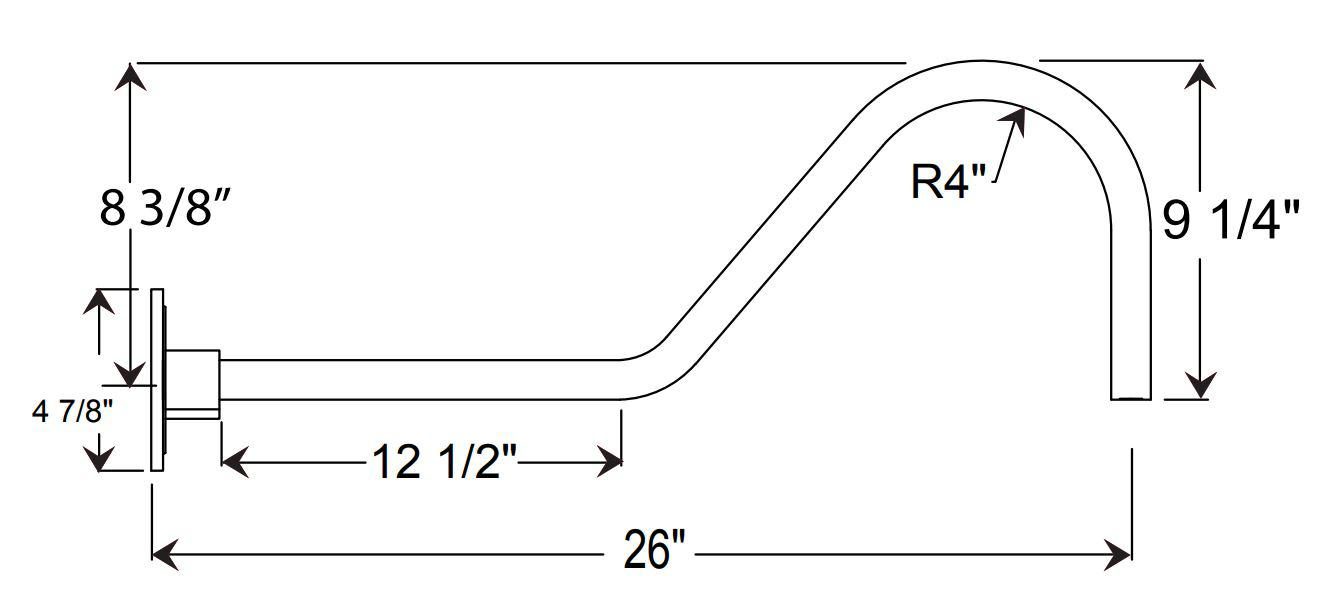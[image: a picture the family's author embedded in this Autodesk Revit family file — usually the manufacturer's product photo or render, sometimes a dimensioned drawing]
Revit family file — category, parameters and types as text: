
# Revit family: Orbitor 100w -12,16 MB
name_source: partatom
category: Lighting Fixtures
units: mm (PartAtom-declared; Revit-internal decimal feet)

## family parameters
Always vertical = Yes
Cut with Voids When Loaded = No
Light Source = Yes
OmniClass Number = 23.80.70.00
OmniClass Title = Lighting
Part Type = Normal
Room Calculation Point = No
Round Connector Dimension = Use Diameter
Shared = No
Work Plane-Based = No

## types (2) — shared parameters
Apparent Load = 100 VA
Body Colour = Spun aluminium
Body Material = body
CRI = >90
Color Filter = 16777215
Construction Material = Heavy Duty spun aluminum.
Default Elevation = 0' - 0"
Description = 120-277 Voltage
Dimming = 1%
Dimming Lamp Color Temperature Shift = <None>
Efficiency = 65-125 lumens per watt
INSIDE BODY = INSIDE BODY
Lamp = MB
Life = L70 50,000 hours
Load Classification = Lighting
Manufacturer = ANP Lighting
Power Factor = 1
Tilt Angle = 90.00°
URL = https://www.anplighting.com
Voltage = 277 V
Warranty = 5 year limited warranty
Wattage Comments = 100W Max

## per-type parameters (varying)
| type | Fixture Diameter | Fixture Height | ORB12 | ORB16 | Photometric Web File | Weight |
| ORB12 | 1' - 0" | 0' - 9 1/2" | Yes | No | ORB12CLM010LDDW40K.IES | 4.0 lbs |
| ORB16 | 1' - 4" | 0' - 10 1/2" | No | Yes | ORB16CLM016LDDW40K.IES | 2.0 lbs |

note: column(s) folded — value = type name in every type: Model

## geometry (parser evidence)
native form markers: Sweep x28
no freeform markers — native parametric forms only
